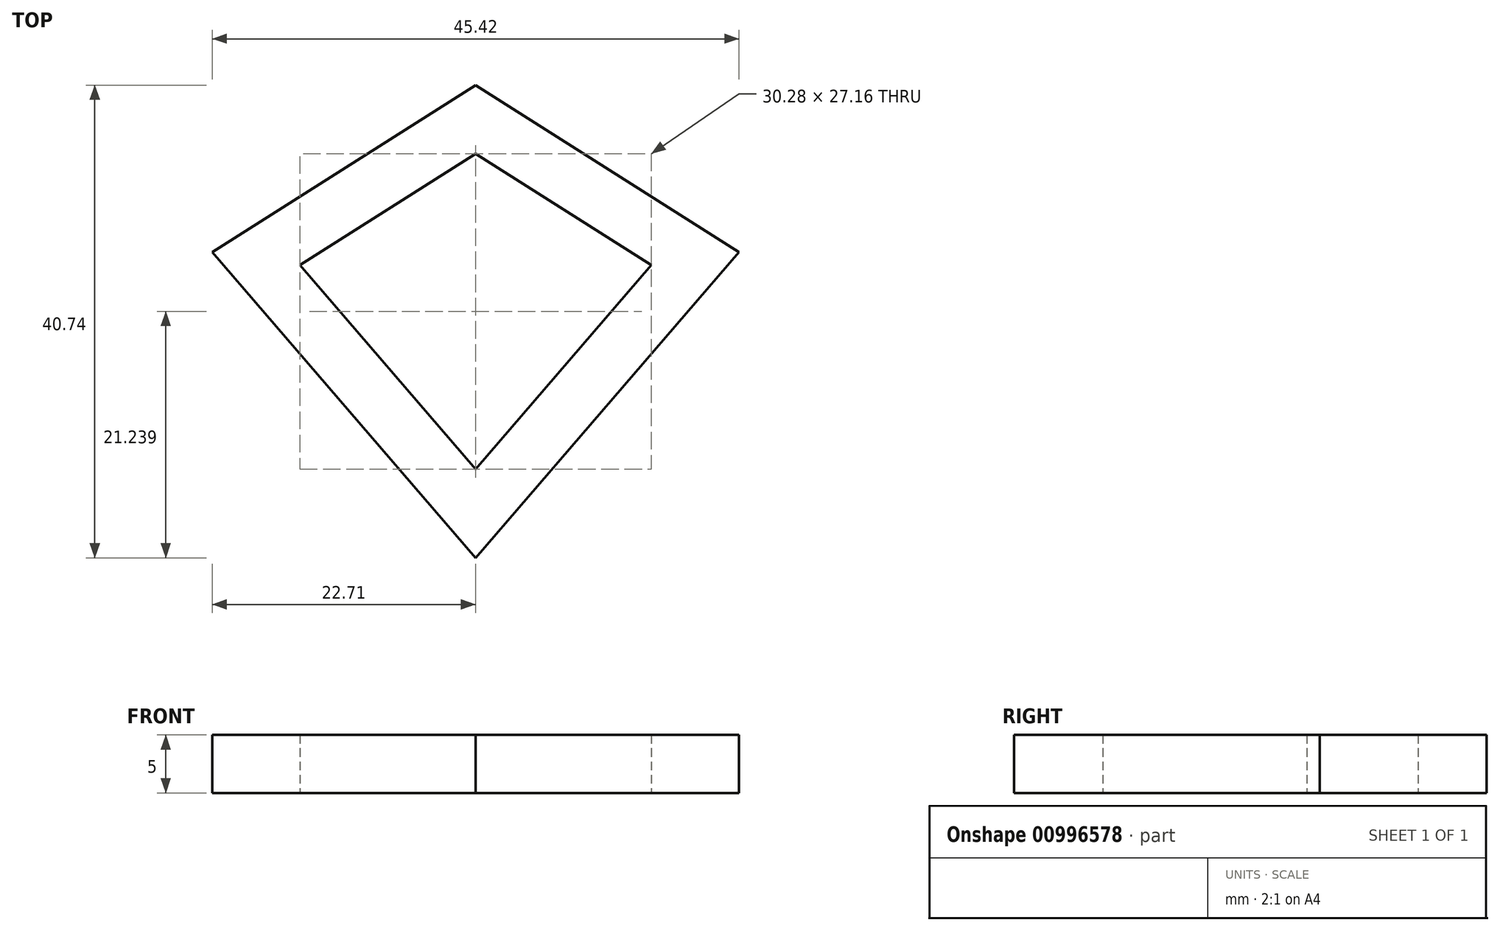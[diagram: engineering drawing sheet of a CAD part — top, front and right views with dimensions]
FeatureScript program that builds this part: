
annotation { "Feature Type Name" : "Feature", "Feature Type Description" : "" }
export const myFeature = defineFeature(function(context is Context, id is Id, definition is map)
    precondition{}
    {
        {
            var Q0;
            Q0=qCreatedBy(makeId("Top.planeOp"),FACE);
            var sketch = newSketch(context, id + "F0", { "sketchPlane" : qUnion([Q0])});
            skLineSegment(sketch, "E0", {"start": v(-22.7, 3.37) * mm, "end": v(0, 17.76) * mm});
            skLineSegment(sketch, "E1", {"start": v(0, 17.76) * mm, "end": v(22.7, 3.37) * mm});
            skLineSegment(sketch, "E2", {"start": v(22.7, 3.37) * mm, "end": v(0, -22.98) * mm});
            skLineSegment(sketch, "E3", {"start": v(0, -22.98) * mm, "end": v(-22.7, 3.37) * mm});
            skCircle(sketch, "E4", {"center": v(0, 0) * mm, "radius": 15 * mm, "construction": true});
            skCircle(sketch, "E5", {"center": v(0, 0) * mm, "radius": 10 * mm, "construction": true});
            skLineSegment(sketch, "E6", {"start": v(0, 11.84) * mm, "end": v(-15.14, 2.25) * mm});
            skLineSegment(sketch, "E7", {"start": v(-15.14, 2.25) * mm, "end": v(0, -15.32) * mm});
            skLineSegment(sketch, "E8", {"start": v(0, -15.32) * mm, "end": v(15.14, 2.25) * mm});
            skLineSegment(sketch, "E9", {"start": v(15.14, 2.25) * mm, "end": v(0, 11.84) * mm});
            skSolve(sketch);
        }
        {
            var Q0;
            Q0=makeQuery(id+"F0.imprint","IMPRINT",FACE,{"disambiguationData":[TD([[makeQuery(id+"F0.imprint","IMPRINT",EDGE,{"derivedFrom":sQuery(id+"F0.wireOp",EDGE,"E0")}),-1.0]])]});
            extrude(context, id + "F1", {"entities" : qUnion([Q0]), "depth" : 5 * mm, "offsetDistance" : 25 * mm});
        }
    });
